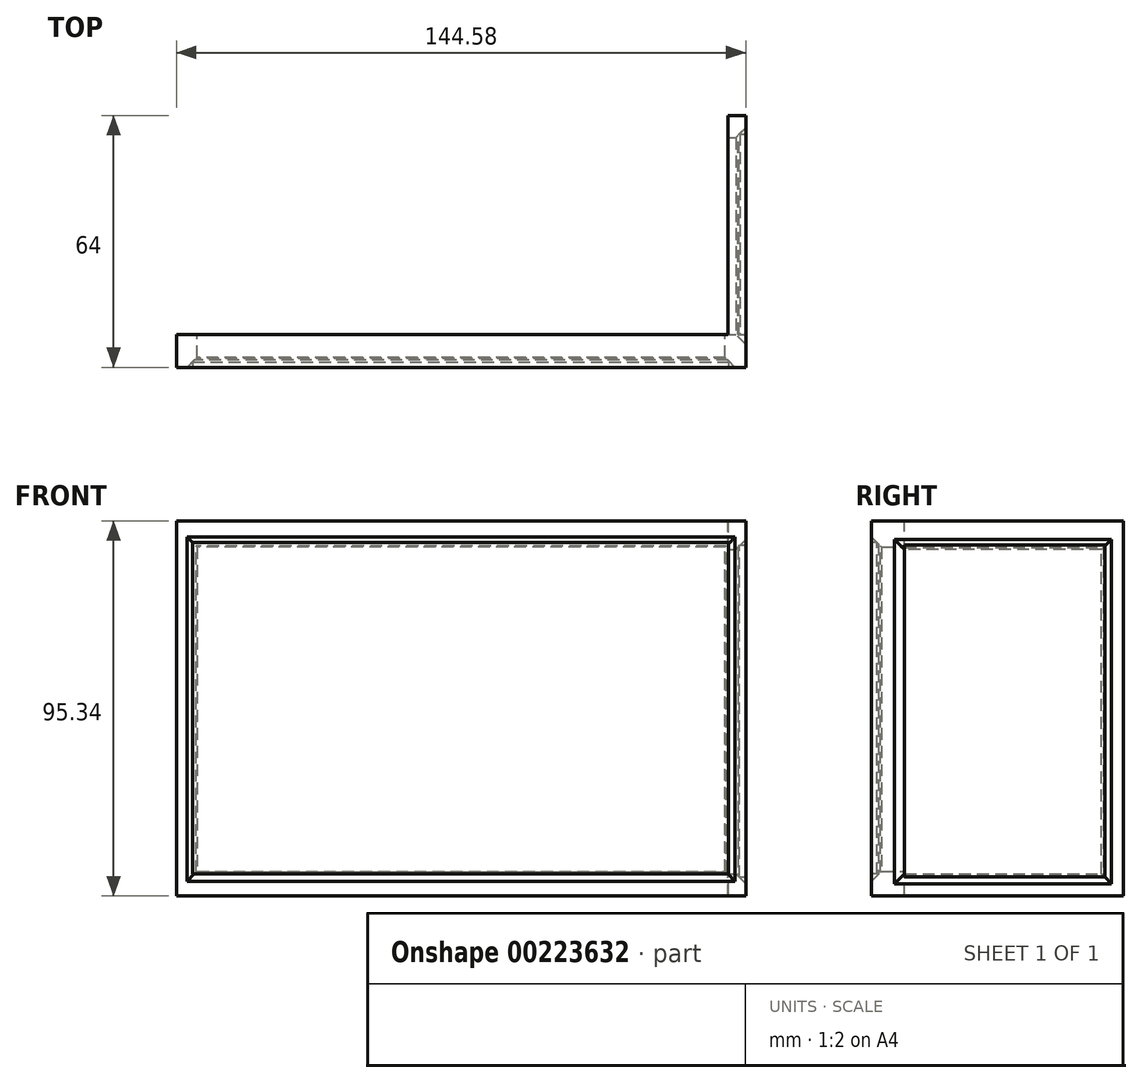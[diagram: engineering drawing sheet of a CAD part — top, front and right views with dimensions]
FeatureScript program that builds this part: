
annotation { "Feature Type Name" : "Feature", "Feature Type Description" : "" }
export const myFeature = defineFeature(function(context is Context, id is Id, definition is map)
    precondition{}
    {
        {
            var Q0;
            Q0=qCreatedBy(makeId("Front.planeOp"),FACE);
            var sketch = newSketch(context, id + "F0", { "sketchPlane" : qUnion([Q0])});
            skLineSegment(sketch, "E0.bottom", {"start": v(-85.5, 39.12) * mm, "end": v(59.07, 39.12) * mm});
            skLineSegment(sketch, "E0.top", {"start": v(-85.5, -56.22) * mm, "end": v(59.07, -56.22) * mm});
            skLineSegment(sketch, "E0.left", {"start": v(-85.5, 39.12) * mm, "end": v(-85.5, -56.22) * mm});
            skLineSegment(sketch, "E0.right", {"start": v(59.07, 39.12) * mm, "end": v(59.07, -56.22) * mm});
            skLineSegment(sketch, "E1.bottom", {"start": v(-80.29, 32.47) * mm, "end": v(53.85, 32.47) * mm});
            skLineSegment(sketch, "E1.top", {"start": v(-80.29, -49.9) * mm, "end": v(53.85, -49.9) * mm});
            skLineSegment(sketch, "E1.left", {"start": v(-80.29, 32.47) * mm, "end": v(-80.29, -49.9) * mm});
            skLineSegment(sketch, "E1.right", {"start": v(53.85, 32.47) * mm, "end": v(53.85, -49.9) * mm});
            skSolve(sketch);
        }
        {
            var Q0;
            Q0 = qSketchRegion(id + "F0", true);
            extrude(context, id + "F1", {"entities" : qUnion([Q0]), "depth" : 8.38 * mm});
        }
        {
            var Q0;
            Q0=makeQuery(id+"F1.opExtrude","SWEPT_FACE",FACE,{"disambiguationData":[OSD([sQuery(id+"F0.wireOp",EDGE,"E0.right")])]});
            var sketch = newSketch(context, id + "F2", { "sketchPlane" : qUnion([Q0])});
            skLineSegment(sketch, "E2.bottom", {"start": v(-8.38, 39.12) * mm, "end": v(55.62, 39.12) * mm});
            skLineSegment(sketch, "E2.top", {"start": v(-8.38, -56.22) * mm, "end": v(55.62, -56.22) * mm});
            skLineSegment(sketch, "E2.left", {"start": v(-8.38, 39.12) * mm, "end": v(-8.38, -56.22) * mm});
            skLineSegment(sketch, "E2.right", {"start": v(55.62, 39.12) * mm, "end": v(55.62, -56.22) * mm});
            skLineSegment(sketch, "E3.bottom", {"start": v(0, 31.82) * mm, "end": v(49.99, 31.82) * mm});
            skLineSegment(sketch, "E3.top", {"start": v(0, -50.53) * mm, "end": v(49.99, -50.53) * mm});
            skLineSegment(sketch, "E3.left", {"start": v(0, 31.82) * mm, "end": v(0, -50.53) * mm});
            skLineSegment(sketch, "E3.right", {"start": v(49.99, 31.82) * mm, "end": v(49.99, -50.53) * mm});
            skSolve(sketch);
        }
        {
            var Q0;
            Q0 = qSketchRegion(id + "F2", true);
            extrude(context, id + "F3", {"entities" : qUnion([Q0]), "operationType" : NewBodyOperationType.ADD, "oppositeDirection" : true, "depth" : 4.57 * mm});
        }
        {
            var Q0;
            Q0=makeQuery(id+"F1.opExtrude","CAP_EDGE",EDGE,{"disambiguationData":[OSD([sQuery(id+"F0.wireOp",EDGE,"E0.right")])],"isStart":true});
            var Q1;
            Q1=makeQuery(id+"F3.opExtrude","CAP_EDGE",EDGE,{"disambiguationData":[OSD([sQuery(id+"F2.wireOp",EDGE,"E3.bottom")])],"isStart":true});
            var Q2;
            Q2=makeQuery(id+"F3.opExtrude","CAP_EDGE",EDGE,{"disambiguationData":[OSD([sQuery(id+"F2.wireOp",EDGE,"E3.right")])],"isStart":true});
            var Q3;
            Q3=makeQuery(id+"F3.opExtrude","CAP_EDGE",EDGE,{"disambiguationData":[OSD([sQuery(id+"F2.wireOp",EDGE,"E3.top")])],"isStart":true});
            chamfer(context, id + "F4", {"entities" : qUnion([Q0, Q1, Q2, Q3]), "width" : 2.54 * mm, "tangentPropagation" : true});
        }
        {
            var Q0;
            Q0=makeQuery(id+"F3.boolean.opBoolean","MERGE",FACE,{"derivedFrom":[makeQuery(id+"F1.opExtrude","SWEPT_FACE",FACE,{"disambiguationData":[OSD([sQuery(id+"F0.wireOp",EDGE,"E0.right")])]}),makeQuery(id+"F3.opExtrude","CAP_FACE",FACE,{"disambiguationData":[OSD([sQuery(id+"F2.wireOp",EDGE,"E2.bottom"),sQuery(id+"F2.wireOp",EDGE,"E2.top"),sQuery(id+"F2.wireOp",EDGE,"E2.left"),sQuery(id+"F2.wireOp",EDGE,"E2.right"),sQuery(id+"F2.wireOp",EDGE,"E3.bottom"),sQuery(id+"F2.wireOp",EDGE,"E3.top"),sQuery(id+"F2.wireOp",EDGE,"E3.left"),sQuery(id+"F2.wireOp",EDGE,"E3.right")])],"isStart":true})]});
            var sketch = newSketch(context, id + "F5", { "sketchPlane" : qUnion([Q0])});
            skLineSegment(sketch, "E4.bottom", {"start": v(0, 32.93) * mm, "end": v(50.9, 32.93) * mm});
            skLineSegment(sketch, "E4.top", {"start": v(0, -51.36) * mm, "end": v(50.9, -51.36) * mm});
            skLineSegment(sketch, "E4.left", {"start": v(0, 32.93) * mm, "end": v(0, -51.36) * mm});
            skLineSegment(sketch, "E4.right", {"start": v(50.9, 32.93) * mm, "end": v(50.9, -51.36) * mm});
            skSolve(sketch);
        }
        {
            var Q0;
            Q0 = qSketchRegion(id + "F5", true);
            extrude(context, id + "F6", {"entities" : qUnion([Q0]), "operationType" : NewBodyOperationType.ADD, "oppositeDirection" : true, "depth" : 2.03 * mm});
        }
        {
            var Q0;
            Q0=makeQuery(id+"F1.opExtrude","CAP_EDGE",EDGE,{"disambiguationData":[OSD([sQuery(id+"F0.wireOp",EDGE,"E1.bottom")])],"isStart":false});
            var Q1;
            Q1=makeQuery(id+"F1.opExtrude","CAP_EDGE",EDGE,{"disambiguationData":[OSD([sQuery(id+"F0.wireOp",EDGE,"E1.left")])],"isStart":false});
            var Q2;
            Q2=makeQuery(id+"F1.opExtrude","CAP_EDGE",EDGE,{"disambiguationData":[OSD([sQuery(id+"F0.wireOp",EDGE,"E1.top")])],"isStart":false});
            var Q3;
            Q3=makeQuery(id+"F1.opExtrude","CAP_EDGE",EDGE,{"disambiguationData":[OSD([sQuery(id+"F0.wireOp",EDGE,"E1.right")])],"isStart":false});
            chamfer(context, id + "F7", {"entities" : qUnion([Q0, Q1, Q2, Q3]), "width" : 2.54 * mm, "tangentPropagation" : true});
        }
        {
            var Q0;
            Q0=makeQuery(id+"F1.opExtrude","CAP_FACE",FACE,{"disambiguationData":[OSD([sQuery(id+"F0.wireOp",EDGE,"E0.bottom"),sQuery(id+"F0.wireOp",EDGE,"E0.top"),sQuery(id+"F0.wireOp",EDGE,"E0.left"),sQuery(id+"F0.wireOp",EDGE,"E0.right"),sQuery(id+"F0.wireOp",EDGE,"E1.bottom"),sQuery(id+"F0.wireOp",EDGE,"E1.top"),sQuery(id+"F0.wireOp",EDGE,"E1.left"),sQuery(id+"F0.wireOp",EDGE,"E1.right")])],"isStart":false});
            var sketch = newSketch(context, id + "F8", { "sketchPlane" : qUnion([Q0])});
            skLineSegment(sketch, "E5.bottom", {"start": v(-81.47, 33.66) * mm, "end": v(54.65, 33.66) * mm});
            skLineSegment(sketch, "E5.top", {"start": v(-81.47, -50.63) * mm, "end": v(54.65, -50.63) * mm});
            skLineSegment(sketch, "E5.left", {"start": v(-81.47, 33.66) * mm, "end": v(-81.47, -50.63) * mm});
            skLineSegment(sketch, "E5.right", {"start": v(54.65, 33.66) * mm, "end": v(54.65, -50.63) * mm});
            skSolve(sketch);
        }
        {
            var Q0;
            Q0 = qSketchRegion(id + "F8", true);
            extrude(context, id + "F9", {"entities" : qUnion([Q0]), "operationType" : NewBodyOperationType.ADD, "oppositeDirection" : true, "depth" : 2.3 * mm});
        }
    });
